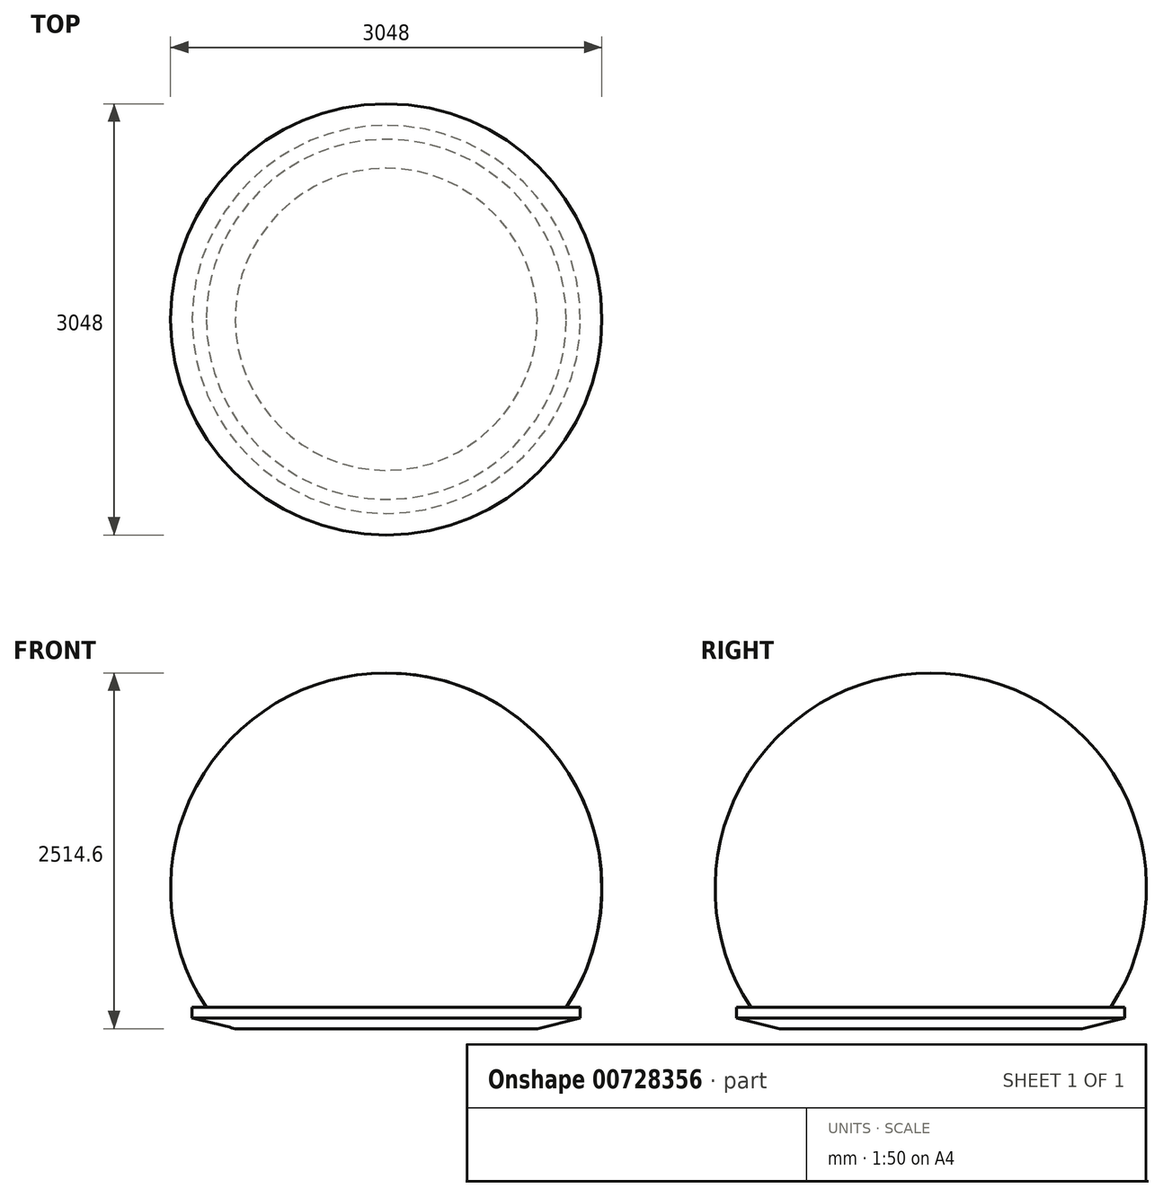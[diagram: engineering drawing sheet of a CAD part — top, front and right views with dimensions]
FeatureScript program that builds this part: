
annotation { "Feature Type Name" : "Feature", "Feature Type Description" : "" }
export const myFeature = defineFeature(function(context is Context, id is Id, definition is map)
    precondition{}
    {
        {
            var Q0;
            Q0=qCreatedBy(makeId("Top.planeOp"),FACE);
            var sketch = newSketch(context, id + "F0", { "sketchPlane" : qUnion([Q0])});
            skCircle(sketch, "E0.cCircle", {"center": v(0, 0) * mm, "radius": 1067.47 * mm, "construction": true});
            skLineSegment(sketch, "E0.0", {"start": v(-329.87, 1015.22) * mm, "end": v(329.87, 1015.22) * mm});
            skLineSegment(sketch, "E0.1", {"start": v(329.87, 1015.22) * mm, "end": v(863.6, 627.44) * mm});
            skLineSegment(sketch, "E0.2", {"start": v(863.6, 627.44) * mm, "end": v(1067.47, 0) * mm});
            skLineSegment(sketch, "E0.3", {"start": v(1067.47, 0) * mm, "end": v(863.6, -627.44) * mm});
            skLineSegment(sketch, "E0.4", {"start": v(863.6, -627.44) * mm, "end": v(329.87, -1015.22) * mm});
            skLineSegment(sketch, "E0.5", {"start": v(329.87, -1015.22) * mm, "end": v(-329.87, -1015.22) * mm});
            skLineSegment(sketch, "E0.6", {"start": v(-329.87, -1015.22) * mm, "end": v(-863.6, -627.44) * mm});
            skLineSegment(sketch, "E0.7", {"start": v(-863.6, -627.44) * mm, "end": v(-1067.47, 0) * mm});
            skLineSegment(sketch, "E0.8", {"start": v(-1067.47, 0) * mm, "end": v(-863.6, 627.44) * mm});
            skLineSegment(sketch, "E0.9", {"start": v(-863.6, 627.44) * mm, "end": v(-329.87, 1015.22) * mm});
            skPoint(sketch, "E1", {"position": v(0, 1015.22) * mm});
            skSolve(sketch);
        }
        {
            var Q0;
            Q0=qCreatedBy(makeId("Front.planeOp"),FACE);
            var sketch = newSketch(context, id + "F1", { "sketchPlane" : qUnion([Q0])});
            skLineSegment(sketch, "E2", {"start": v(0, 0) * mm, "end": v(0, 152.4) * mm});
            skLineSegment(sketch, "E3", {"start": v(0, 152.4) * mm, "end": v(1371.6, 152.4) * mm});
            skLineSegment(sketch, "E4", {"start": v(1371.6, 152.4) * mm, "end": v(1371.6, 76.2) * mm});
            skLineSegment(sketch, "E5", {"start": v(1371.6, 76.2) * mm, "end": v(1067.47, 0) * mm});
            skLineSegment(sketch, "E6", {"start": v(1067.47, 0) * mm, "end": v(0, 0) * mm});
            skPoint(sketch, "E7.0", {"position": v(1067.47, 0) * mm});
            skSolve(sketch);
        }
        {
            var Q0;
            Q0=qCreatedBy(makeId("Front.planeOp"),FACE);
            var sketch = newSketch(context, id + "F2", { "sketchPlane" : qUnion([Q0])});
            skLineSegment(sketch, "E8.0", {"start": v(0, 152.4) * mm, "end": v(1371.6, 152.4) * mm, "construction": true});
            skPoint(sketch, "E8.1", {"position": v(0, 152.4) * mm});
            skLineSegment(sketch, "E9", {"start": v(0, 152.4) * mm, "end": v(0, 2514.6) * mm});
            skPoint(sketch, "E10", {"position": v(0, 990.6) * mm});
            skArc(sketch, "E11", {"start": v(1272.8, 152.4) * mm, "mid": v(1341.64, 1713.5) * mm, "end": v(0, 2514.6) * mm});
            skLineSegment(sketch, "E12", {"start": v(0, 152.4) * mm, "end": v(1272.8, 152.4) * mm});
            skSolve(sketch);
        }
        {
            var Q0;
            Q0 = qSketchRegion(id + "F1", true);
            var Q1;
            Q1=sQuery(id+"F2.wireOp",EDGE,"E9");
            revolve(context, id + "F3", {"surfaceOperationType" : NewSurfaceOperationType.NEW, "entities" : qUnion([Q0]), "axis" : qUnion([Q1]), "revolveType" : RevolveType.FULL});
        }
        {
            var Q0;
            Q0 = qSketchRegion(id + "F2", true);
            var Q1;
            Q1=sQuery(id+"F2.wireOp",EDGE,"E9");
            revolve(context, id + "F4", {"surfaceOperationType" : NewSurfaceOperationType.NEW, "entities" : qUnion([Q0]), "axis" : qUnion([Q1]), "revolveType" : RevolveType.FULL});
        }
    });
